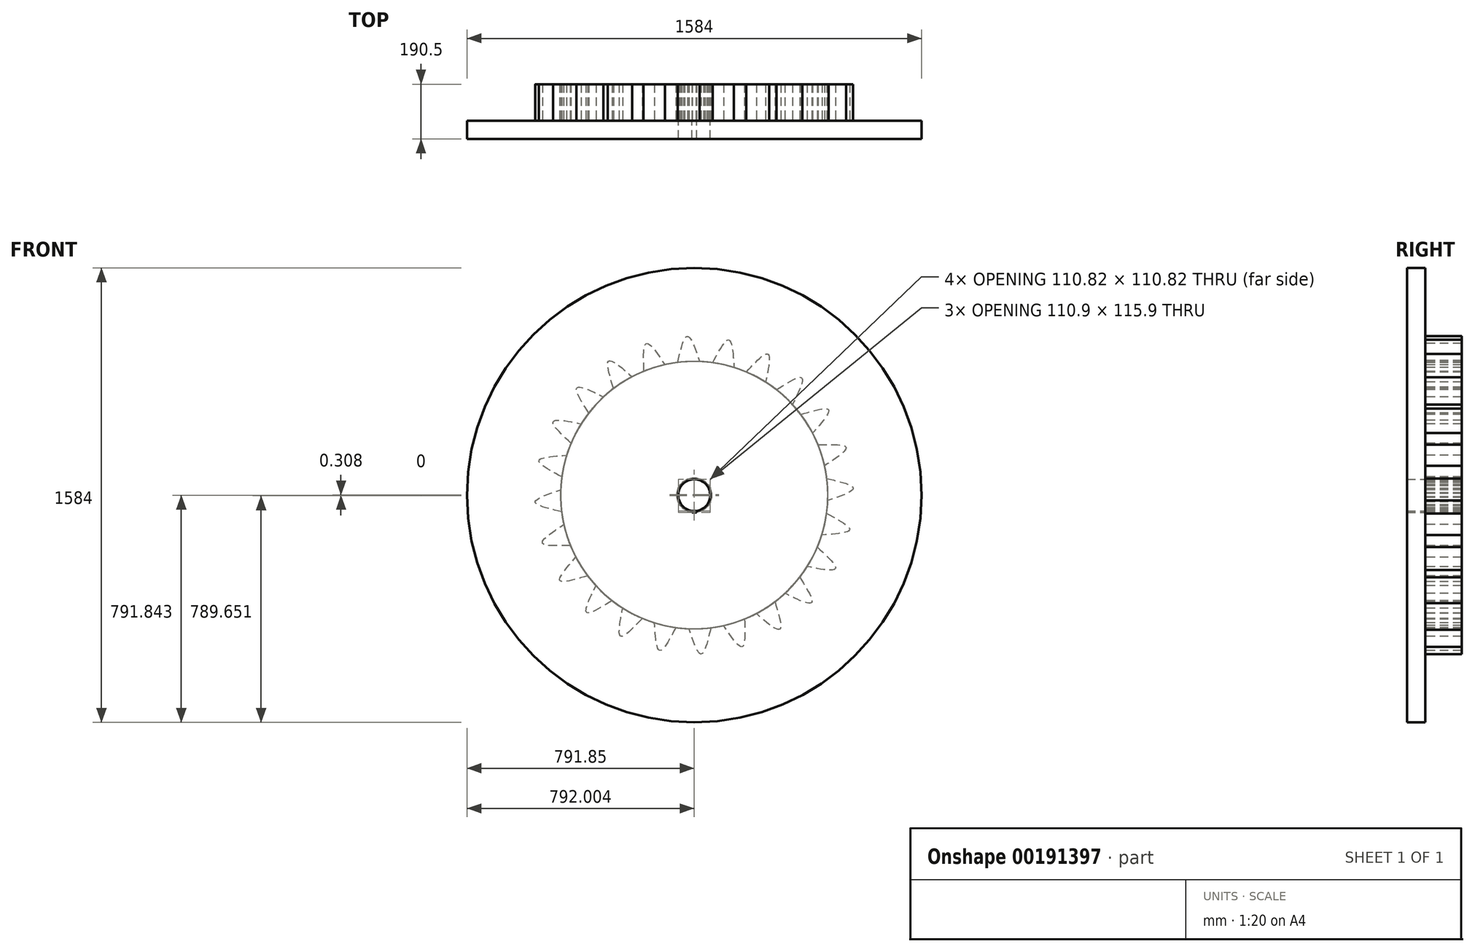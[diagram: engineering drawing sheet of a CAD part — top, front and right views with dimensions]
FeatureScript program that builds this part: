
annotation { "Feature Type Name" : "Feature", "Feature Type Description" : "" }
export const myFeature = defineFeature(function(context is Context, id is Id, definition is map)
    precondition{}
    {
        {
            var Q0;
            Q0=qCreatedBy(makeId("Front.planeOp"),FACE);
            var sketch = newSketch(context, id + "F0", { "sketchPlane" : qUnion([Q0])});
            skCircle(sketch, "E0", {"center": v(-50.77, 60.3) * mm, "radius": 792 * mm});
            skArc(sketch, "E1", {"start": v(-108.35, 522.73) * mm, "mid": v(-31.22, -405.3) * mm, "end": v(-32.15, 525.93) * mm});
            skFitSpline(sketch, "E2", {"points": [v(-108.35, 522.73) * mm, v(-74.73, 614.23) * mm, v(-32.15, 525.93) * mm], "startDerivative": vector(62.78, 274.34) * mm, "endDerivative": vector(89.46, -267.7) * mm});
            skArc(sketch, "E3", {"start": v(-42.51, 5.3) * mm, "mid": v(-50.77, 115.9) * mm, "end": v(-59.02, 5.3) * mm});
            skLineSegment(sketch, "E4.bottom", {"start": v(-42.51, 0) * mm, "end": v(-59.02, 0.2) * mm});
            skLineSegment(sketch, "E4.left", {"start": v(-42.51, 0) * mm, "end": v(-42.51, 5.3) * mm});
            skLineSegment(sketch, "E4.right", {"start": v(-59.02, 0.2) * mm, "end": v(-59.02, 5.3) * mm});
            skPoint(sketch, "E4.middle", {"position": v(-50.77, 4.7) * mm});
            skPoint(sketch, "E5.orphan", {"position": v(-59.02, 9.39) * mm});
            skPoint(sketch, "E6.orphan", {"position": v(-42.51, 9.19) * mm});
            skSolve(sketch);
        }
        {
            var Q0;
            Q0=makeQuery(id+"F0.imprint","IMPRINT",FACE,{"disambiguationData":[TD([[makeQuery(id+"F0.imprint","IMPRINT",EDGE,{"derivedFrom":sQuery(id+"F0.wireOp",EDGE,"E0")}),1.0]])]});
            var Q1;
            Q1=makeQuery(id+"F0.imprint","IMPRINT",FACE,{"disambiguationData":[TD([[makeQuery(id+"F0.imprint","IMPRINT",EDGE,{"derivedFrom":sQuery(id+"F0.wireOp",EDGE,"E1")}),1.0]])]});
            extrude(context, id + "F1", {"entities" : qUnion([Q0, Q1]), "depth" : 63.5 * mm});
        }
        {
            var Q0;
            Q0=makeQuery(id+"F0.imprint","IMPRINT",FACE,{"disambiguationData":[TD([[makeQuery(id+"F0.imprint","IMPRINT",EDGE,{"derivedFrom":sQuery(id+"F0.wireOp",EDGE,"E1")}),1.0]])]});
            extrude(context, id + "F2", {"entities" : qUnion([Q0]), "oppositeDirection" : true, "depth" : 127 * mm});
        }
        {
            var Q0;
            Q0=makeQuery(id+"F2.opExtrude","SWEPT_BODY",BODY,{"disambiguationData":[OSD([sQuery(id+"F0.wireOp",EDGE,"E1"),sQuery(id+"F0.wireOp",EDGE,"E2")])]});
            var Q1;
            Q1=sQuery(id+"F0.wireOp",EDGE,"E0");
            circularPattern(context, id + "F3", {"entities" : qUnion([Q0]), "axis" : qUnion([Q1]), "angle" : 15 * degree, "instanceCount" : 24});
        }
    });
